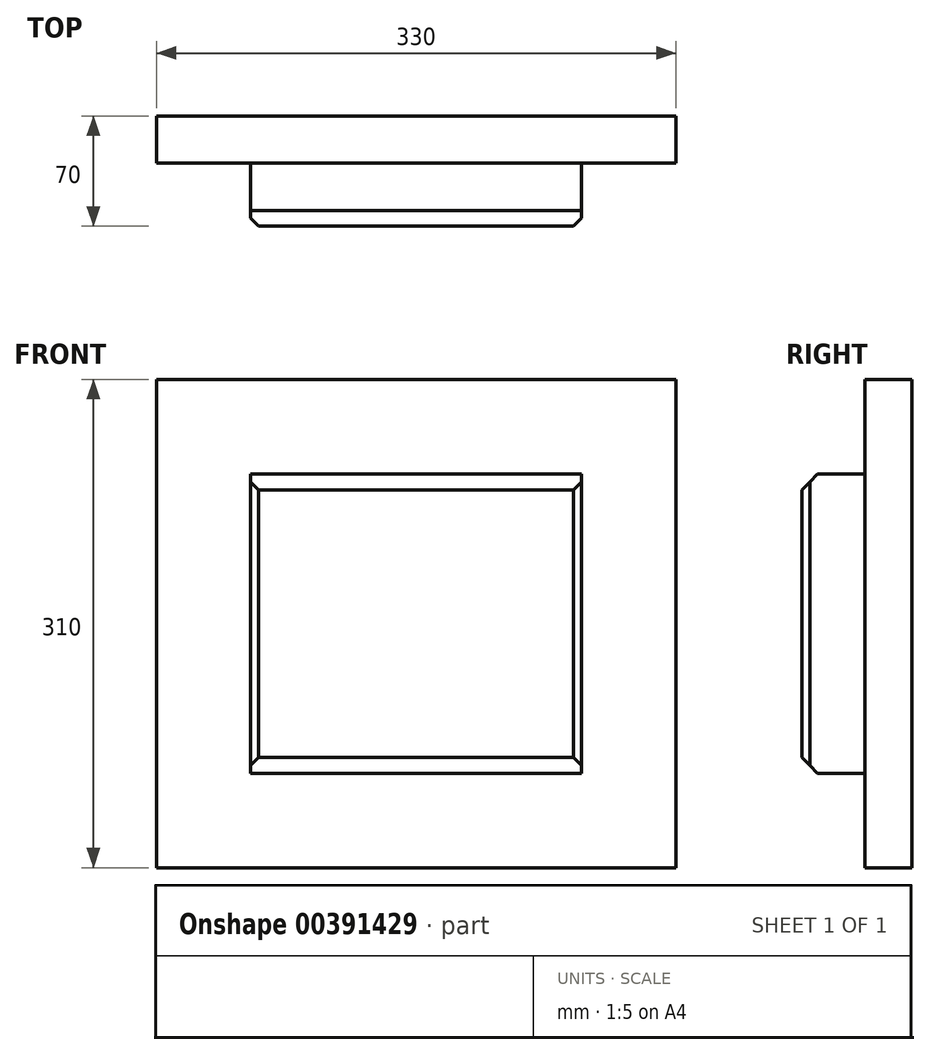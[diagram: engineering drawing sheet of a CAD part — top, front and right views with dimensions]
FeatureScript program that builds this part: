
annotation { "Feature Type Name" : "Feature", "Feature Type Description" : "" }
export const myFeature = defineFeature(function(context is Context, id is Id, definition is map)
    precondition{}
    {
        {
            var Q0;
            Q0=qCreatedBy(makeId("Front.planeOp"),FACE);
            var sketch = newSketch(context, id + "F0", { "sketchPlane" : qUnion([Q0])});
            skLineSegment(sketch, "E0.bottom", {"start": v(102.83, 95) * mm, "end": v(-107.17, 95) * mm});
            skLineSegment(sketch, "E0.top", {"start": v(102.83, -95) * mm, "end": v(-107.17, -95) * mm});
            skLineSegment(sketch, "E0.left", {"start": v(102.83, 95) * mm, "end": v(102.83, -95) * mm});
            skLineSegment(sketch, "E0.right", {"start": v(-107.17, 95) * mm, "end": v(-107.17, -95) * mm});
            skPoint(sketch, "E0.middle", {"position": v(-2.17, 0) * mm});
            skSolve(sketch);
        }
        {
            var Q0;
            Q0 = qSketchRegion(id + "F0", true);
            extrude(context, id + "F1", {"entities" : qUnion([Q0]), "depth" : 40 * mm});
        }
        {
            var Q0;
            Q0=makeQuery(id+"F1.opExtrude","CAP_FACE",FACE,{"disambiguationData":[OSD([sQuery(id+"F0.wireOp",EDGE,"E0.bottom"),sQuery(id+"F0.wireOp",EDGE,"E0.top"),sQuery(id+"F0.wireOp",EDGE,"E0.left"),sQuery(id+"F0.wireOp",EDGE,"E0.right")])],"isStart":true});
            var sketch = newSketch(context, id + "F2", { "sketchPlane" : qUnion([Q0])});
            skLineSegment(sketch, "E1.0", {"start": v(-162.83, -155) * mm, "end": v(167.17, -155) * mm});
            skLineSegment(sketch, "E1.1", {"start": v(-162.83, 155) * mm, "end": v(-162.83, -155) * mm});
            skLineSegment(sketch, "E1.2", {"start": v(167.17, 155) * mm, "end": v(-162.83, 155) * mm});
            skLineSegment(sketch, "E1.3", {"start": v(167.17, -155) * mm, "end": v(167.17, 155) * mm});
            skSolve(sketch);
        }
        {
            var Q0;
            Q0 = qSketchRegion(id + "F2", true);
            extrude(context, id + "F3", {"entities" : qUnion([Q0]), "operationType" : NewBodyOperationType.ADD, "depth" : 30 * mm});
        }
        {
            var Q0;
            Q0=makeQuery(id+"F1.opExtrude","CAP_EDGE",EDGE,{"disambiguationData":[OSD([sQuery(id+"F0.wireOp",EDGE,"E0.bottom")])],"isStart":false});
            var Q1;
            Q1=makeQuery(id+"F1.opExtrude","CAP_EDGE",EDGE,{"disambiguationData":[OSD([sQuery(id+"F0.wireOp",EDGE,"E0.top")])],"isStart":false});
            chamfer(context, id + "F4", {"entities" : qUnion([Q0, Q1]), "width" : 10 * mm, "tangentPropagation" : true});
        }
        {
            var Q0;
            Q0=makeQuery(id+"F1.opExtrude","CAP_EDGE",EDGE,{"disambiguationData":[OSD([sQuery(id+"F0.wireOp",EDGE,"E0.right")])],"isStart":false});
            var Q1;
            Q1=makeQuery(id+"F1.opExtrude","CAP_EDGE",EDGE,{"disambiguationData":[OSD([sQuery(id+"F0.wireOp",EDGE,"E0.left")])],"isStart":false});
            chamfer(context, id + "F5", {"entities" : qUnion([Q0, Q1]), "width" : 5 * mm, "tangentPropagation" : true});
        }
    });
